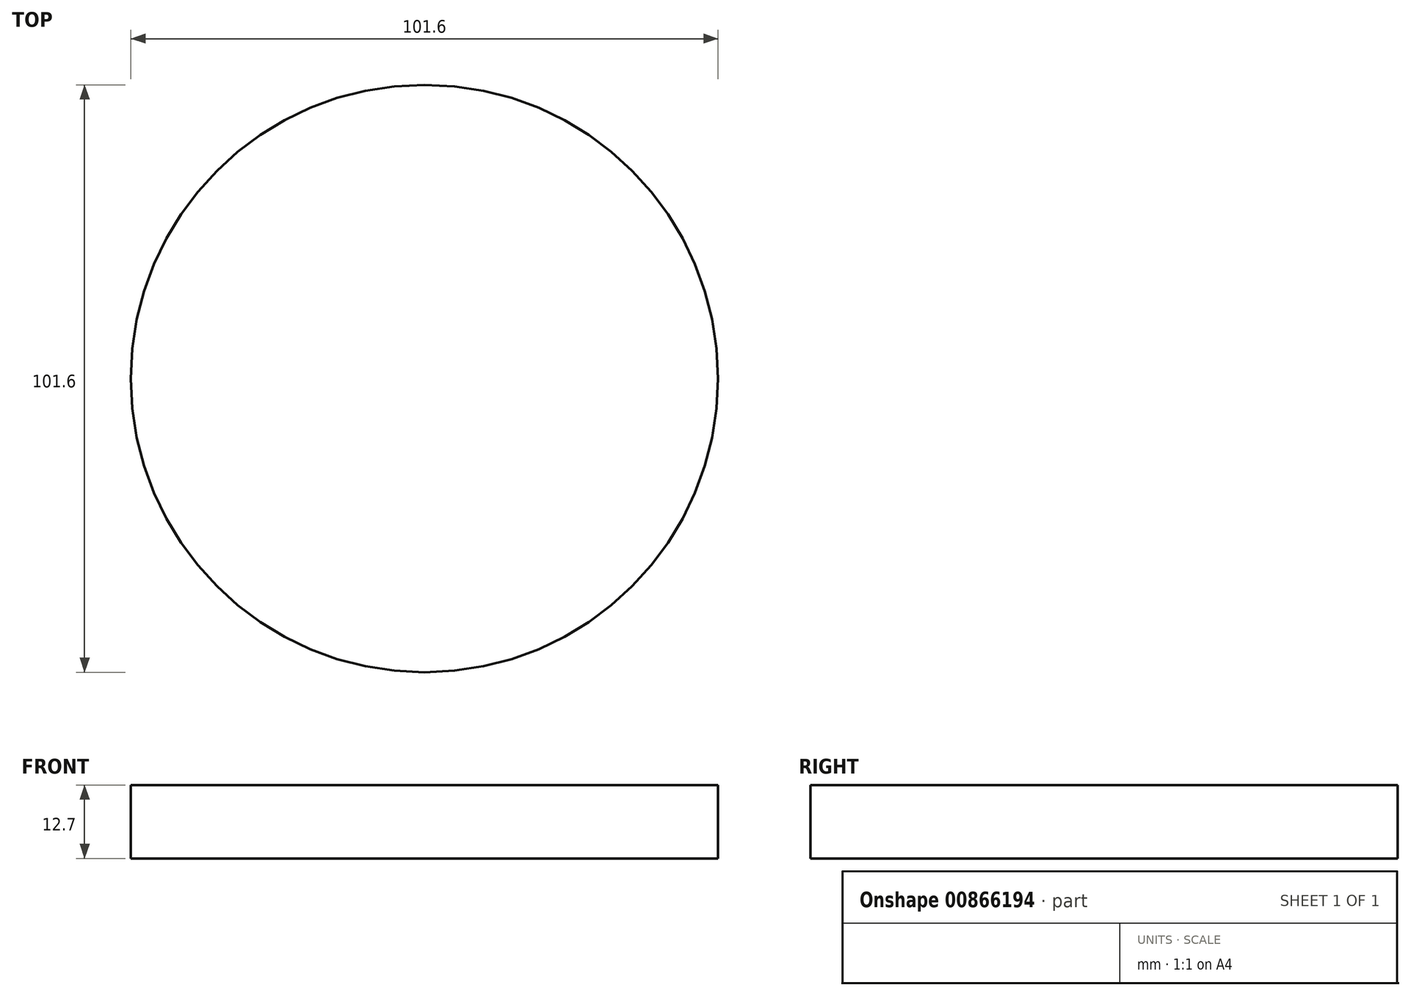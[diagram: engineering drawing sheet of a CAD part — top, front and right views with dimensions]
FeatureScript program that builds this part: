
annotation { "Feature Type Name" : "Feature", "Feature Type Description" : "" }
export const myFeature = defineFeature(function(context is Context, id is Id, definition is map)
    precondition{}
    {
        {
            var Q0;
            Q0=qCreatedBy(makeId("Top.planeOp"),FACE);
            var sketch = newSketch(context, id + "F0", { "sketchPlane" : qUnion([Q0])});
            skCircle(sketch, "E0", {"center": v(0, 0) * mm, "radius": 50.8 * mm});
            skSolve(sketch);
        }
        {
            var Q0;
            Q0=makeQuery(id+"F0.imprint","IMPRINT",FACE,{"disambiguationData":[TD([[makeQuery(id+"F0.imprint","IMPRINT",EDGE,{"derivedFrom":sQuery(id+"F0.wireOp",EDGE,"E0")}),1.0]])]});
            extrude(context, id + "F1", {"entities" : qUnion([Q0]), "depth" : 12.7 * mm, "offsetDistance" : 25.4 * mm});
        }
    });
